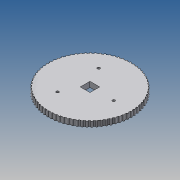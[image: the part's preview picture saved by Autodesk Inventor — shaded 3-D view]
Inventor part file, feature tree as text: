
AUTODESK INVENTOR PART (.ipt)
format: ipt  version: 2017 (Build 210142000, 142)  size: 344,064 bytes
history: native  units: mm
features: other x3, extrude x3, sketch x3
ambient origin geometry x8: Origin, YZ Plane, XZ Plane, XY Plane, X Axis, Y Axis, Z Axis, Center Point
bodies: Body1 (feature_tree)
feature tree (9):
  other  "Sólido1"
  extrude  "Extrusión1"  Depth=6.0mm TaperAngle=0.0deg
  extrude  "Extrusión2"  Depth=5.5mm
  extrude  "Extrusión3"  Depth=14.0mm
  sketch  "Boceto1"  dims[d0=96.81mm d1=6.0mm d2=0.0mm]
  sketch  "Boceto2"  dims[d4=3.0mm d5=0.0mm d6=5.5mm]
  other  "Sólido2"
  sketch  "Boceto3"  dims[d7=3.0mm d8=0.0mm d9=2.2mm d11=72.0mm d20=51.545062mm d21=188.91991mm d22=66.846372mm d24=760.0mm d26=360.0deg d28=3.794046mm d30=83.0mm d31=3.6mm d32=2.5mm d33=14.0mm d34=84.517316mm]
  other  "Sólido3"
